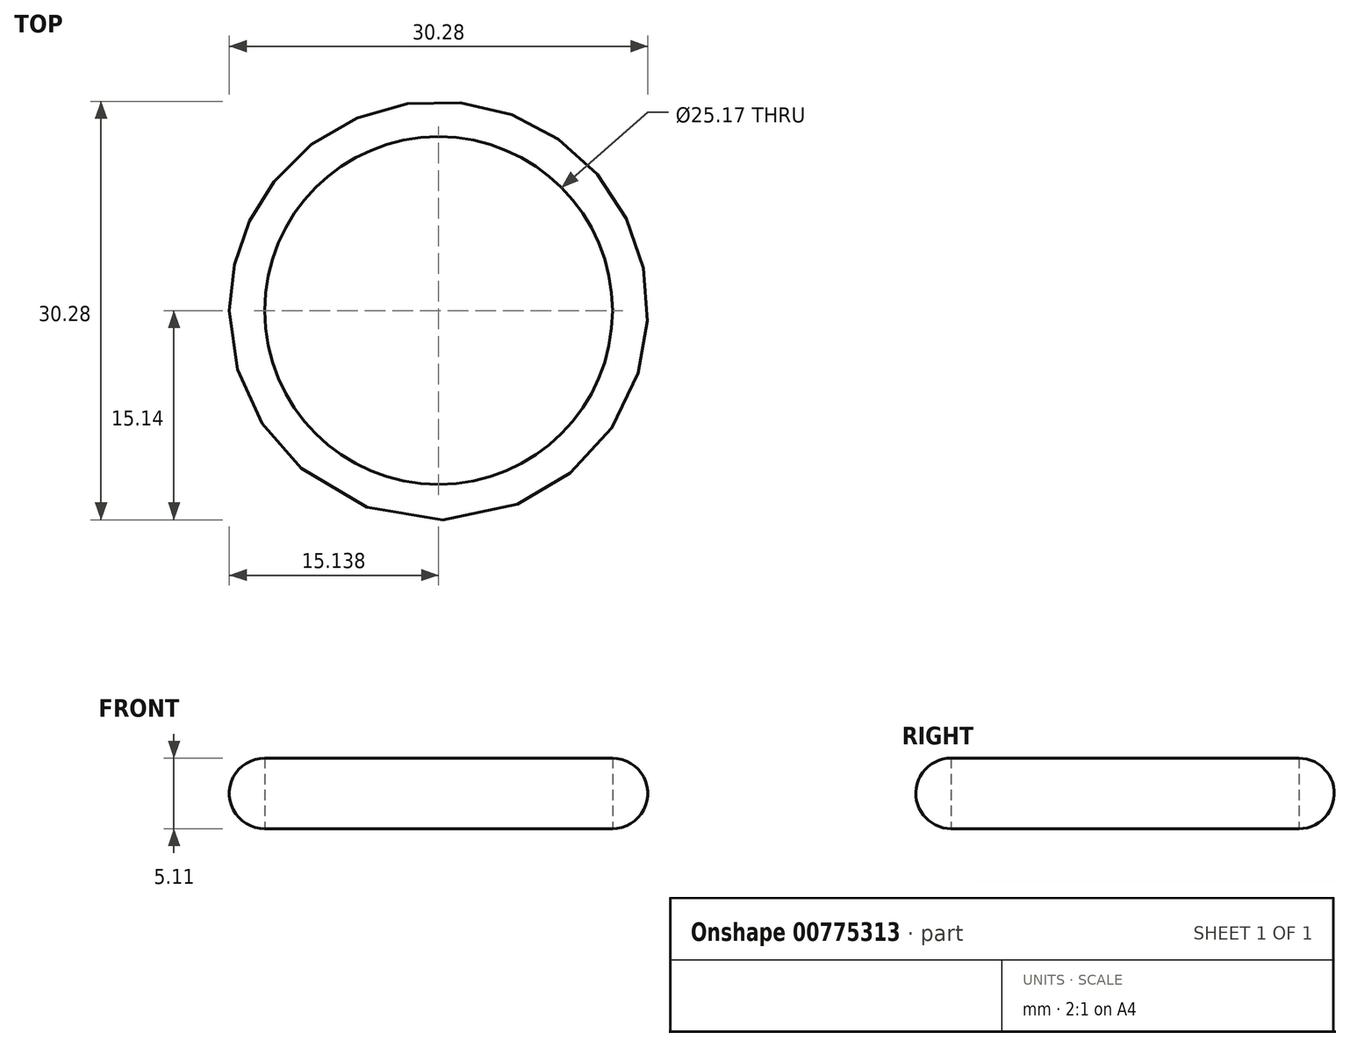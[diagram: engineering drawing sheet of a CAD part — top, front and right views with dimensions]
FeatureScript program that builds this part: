
annotation { "Feature Type Name" : "Feature", "Feature Type Description" : "" }
export const myFeature = defineFeature(function(context is Context, id is Id, definition is map)
    precondition{}
    {
        {
            var Q0;
            Q0=qCreatedBy(makeId("Front.planeOp"),FACE);
            var sketch = newSketch(context, id + "F0", { "sketchPlane" : qUnion([Q0])});
            skLineSegment(sketch, "E0", {"start": v(4.31, -2.72) * mm, "end": v(-8.27, -2.72) * mm});
            skLineSegment(sketch, "E1", {"start": v(-8.27, -2.72) * mm, "end": v(-8.27, 8.8) * mm});
            skLineSegment(sketch, "E2", {"start": v(4.31, -2.72) * mm, "end": v(4.31, 2.4) * mm});
            skArc(sketch, "E3", {"start": v(4.31, -2.72) * mm, "mid": v(6.87, -0.16) * mm, "end": v(4.31, 2.4) * mm});
            skSolve(sketch);
        }
        {
            var Q0;
            Q0 = qSketchRegion(id + "F0", true);
            var Q1;
            Q1=sQuery(id+"F0.wireOp",EDGE,"E1");
            revolve(context, id + "F1", {"surfaceOperationType" : NewSurfaceOperationType.NEW, "entities" : qUnion([Q0]), "axis" : qUnion([Q1]), "revolveType" : RevolveType.FULL});
        }
    });
